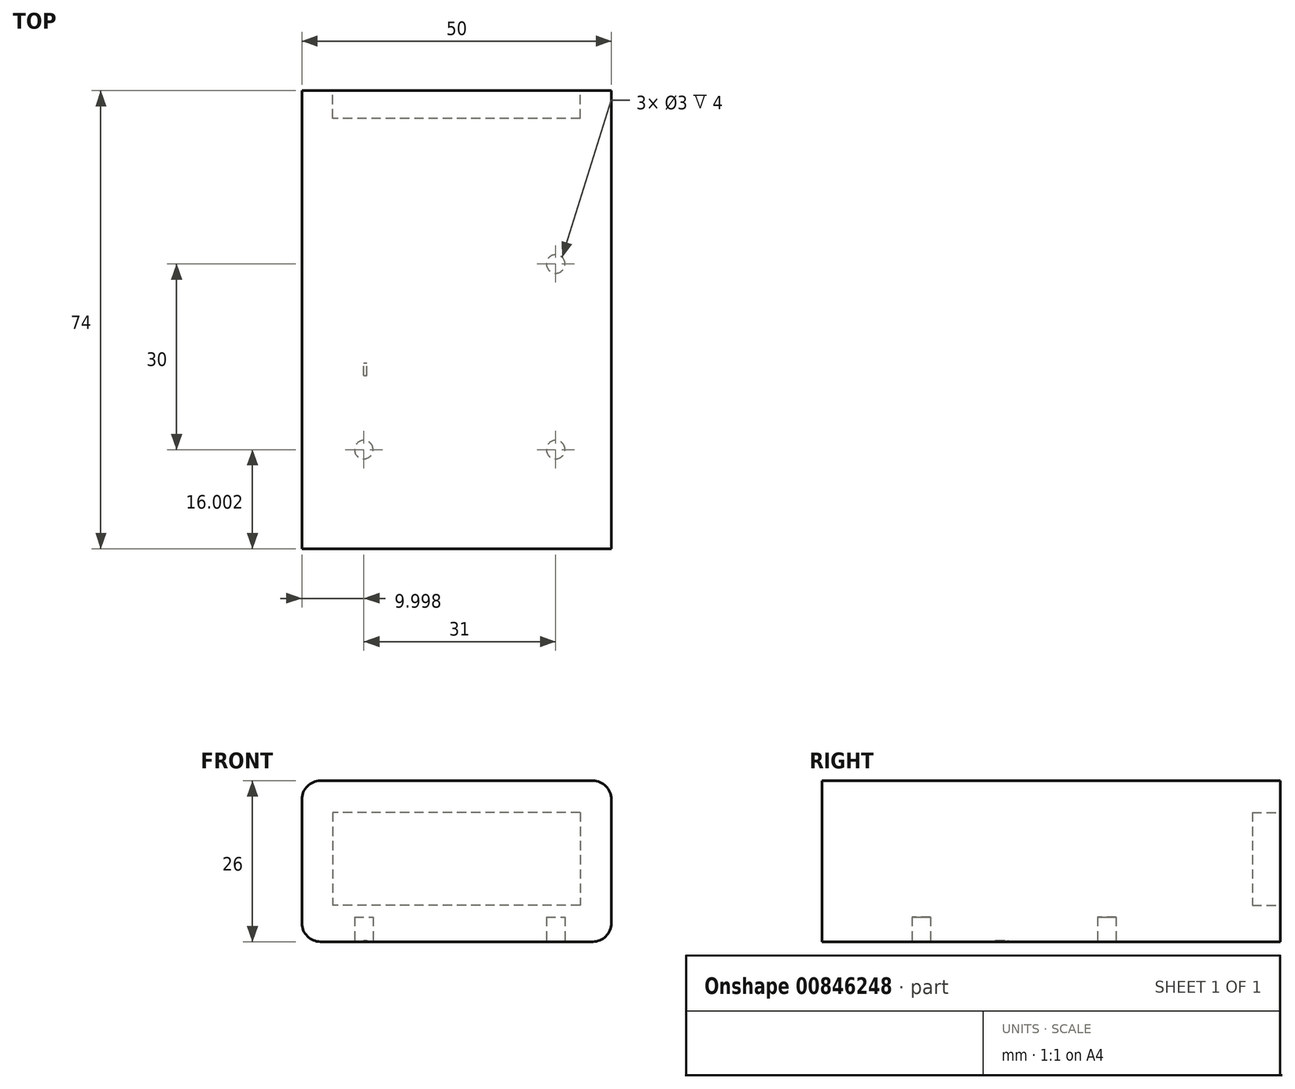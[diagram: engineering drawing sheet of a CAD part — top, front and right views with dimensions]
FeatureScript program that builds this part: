
annotation { "Feature Type Name" : "Feature", "Feature Type Description" : "" }
export const myFeature = defineFeature(function(context is Context, id is Id, definition is map)
    precondition{}
    {
        {
            var Q0;
            Q0=qCreatedBy(makeId("Top.planeOp"),FACE);
            var sketch = newSketch(context, id + "F0", { "sketchPlane" : qUnion([Q0])});
            skLineSegment(sketch, "E0.bottom", {"start": v(-22.9, 37.62) * mm, "end": v(27.1, 37.62) * mm});
            skLineSegment(sketch, "E0.top", {"start": v(-22.9, -36.38) * mm, "end": v(27.1, -36.38) * mm});
            skLineSegment(sketch, "E0.left", {"start": v(-22.9, 37.62) * mm, "end": v(-22.9, -36.38) * mm});
            skLineSegment(sketch, "E0.right", {"start": v(27.1, 37.62) * mm, "end": v(27.1, -36.38) * mm});
            skSolve(sketch);
        }
        {
            var Q0;
            Q0 = qSketchRegion(id + "F0", true);
            extrude(context, id + "F1", {"entities" : qUnion([Q0]), "depth" : 26 * mm, "offsetDistance" : 25 * mm});
        }
        {
            var Q0;
            Q0=makeQuery(id+"F1.opExtrude","SWEPT_FACE",FACE,{"disambiguationData":[OSD([sQuery(id+"F0.wireOp",EDGE,"E0.bottom")])]});
            var sketch = newSketch(context, id + "F2", { "sketchPlane" : qUnion([Q0])});
            skLineSegment(sketch, "E1.bottom", {"start": v(-22.05, 20.89) * mm, "end": v(17.95, 20.89) * mm});
            skLineSegment(sketch, "E1.top", {"start": v(-22.05, 5.89) * mm, "end": v(17.95, 5.89) * mm});
            skLineSegment(sketch, "E1.left", {"start": v(-22.05, 20.89) * mm, "end": v(-22.05, 5.89) * mm});
            skLineSegment(sketch, "E1.right", {"start": v(17.95, 20.89) * mm, "end": v(17.95, 5.89) * mm});
            skSolve(sketch);
        }
        {
            var Q0;
            Q0 = qSketchRegion(id + "F2", true);
            extrude(context, id + "F3", {"entities" : qUnion([Q0]), "operationType" : NewBodyOperationType.REMOVE, "oppositeDirection" : true, "depth" : 4.5 * mm, "offsetDistance" : 25 * mm});
        }
        {
            var Q0;
            Q0=makeQuery(id+"F1.opExtrude","CAP_FACE",FACE,{"disambiguationData":[OSD([sQuery(id+"F0.wireOp",EDGE,"E0.bottom"),sQuery(id+"F0.wireOp",EDGE,"E0.top"),sQuery(id+"F0.wireOp",EDGE,"E0.left"),sQuery(id+"F0.wireOp",EDGE,"E0.right")])],"isStart":true});
            var sketch = newSketch(context, id + "F4", { "sketchPlane" : qUnion([Q0])});
            skLineSegment(sketch, "E2", {"start": v(18.1, -37.62) * mm, "end": v(18.1, -9.62) * mm});
            skLineSegment(sketch, "E3", {"start": v(18.1, -9.62) * mm, "end": v(18.1, 20.38) * mm});
            skLineSegment(sketch, "E4", {"start": v(18.1, 20.38) * mm, "end": v(-12.9, 20.38) * mm});
            skCircle(sketch, "E5", {"center": v(18.1, 20.38) * mm, "radius": 1.5 * mm});
            skCircle(sketch, "E6", {"center": v(-12.9, 20.38) * mm, "radius": 1.5 * mm});
            skCircle(sketch, "E7", {"center": v(18.1, -9.62) * mm, "radius": 1.5 * mm});
            skCircle(sketch, "E8", {"center": v(18.1, -9.62) * mm, "radius": 2.25 * mm});
            skCircle(sketch, "E9", {"center": v(18.1, 20.38) * mm, "radius": 2.25 * mm});
            skCircle(sketch, "E10", {"center": v(-12.9, 20.38) * mm, "radius": 2.25 * mm});
            skLineSegment(sketch, "E11", {"start": v(-12.9, 20.38) * mm, "end": v(-12.9, 8.38) * mm});
            skLineSegment(sketch, "E12.bottom", {"start": v(-12.9, 8.38) * mm, "end": v(-12.4, 8.38) * mm});
            skLineSegment(sketch, "E12.top", {"start": v(-12.9, 6.38) * mm, "end": v(-12.4, 6.38) * mm});
            skLineSegment(sketch, "E12.left", {"start": v(-12.9, 8.38) * mm, "end": v(-12.9, 6.38) * mm});
            skLineSegment(sketch, "E12.right", {"start": v(-12.4, 8.38) * mm, "end": v(-12.4, 6.38) * mm});
            skSolve(sketch);
        }
        {
            var Q0;
            Q0=makeQuery(id+"F1.opExtrude","CAP_EDGE",EDGE,{"disambiguationData":[OSD([sQuery(id+"F0.wireOp",EDGE,"E0.right")])],"isStart":true});
            var Q1;
            Q1=makeQuery(id+"F1.opExtrude","CAP_EDGE",EDGE,{"disambiguationData":[OSD([sQuery(id+"F0.wireOp",EDGE,"E0.right")])],"isStart":false});
            var Q2;
            Q2=makeQuery(id+"F1.opExtrude","CAP_EDGE",EDGE,{"disambiguationData":[OSD([sQuery(id+"F0.wireOp",EDGE,"E0.left")])],"isStart":true});
            var Q3;
            Q3=makeQuery(id+"F1.opExtrude","CAP_EDGE",EDGE,{"disambiguationData":[OSD([sQuery(id+"F0.wireOp",EDGE,"E0.left")])],"isStart":false});
            fillet(context, id + "F5", {"entities" : qUnion([Q0, Q1, Q2, Q3]), "radius" : 3 * mm, "tangentPropagation" : true, "allowEdgeOverflow" : false});
        }
        {
            var Q0;
            {var subQ0=sQuery(id+"F4.wireOp",EDGE,"E4");var subQ1=sQuery(id+"F4.wireOp",EDGE,"E3");var subQ2=makeQuery(id+"F4.imprint","INTERSECT",VERTEX,{"derivedFrom":[subQ1,subQ0]});Q0=makeQuery(id+"F4.imprint","IMPRINT",FACE,{"disambiguationData":[TD([[makeQuery(id+"F4.imprint","IMPRINT",EDGE,{"disambiguationData":[TD([[subQ2,1.0]])],"derivedFrom":subQ1}),-1.0]])]});}
            var Q1;
            {var subQ0=sQuery(id+"F4.wireOp",EDGE,"E4");var subQ1=sQuery(id+"F4.wireOp",EDGE,"E3");var subQ2=makeQuery(id+"F4.imprint","INTERSECT",VERTEX,{"derivedFrom":[subQ1,subQ0]});Q1=makeQuery(id+"F4.imprint","IMPRINT",FACE,{"disambiguationData":[TD([[makeQuery(id+"F4.imprint","IMPRINT",EDGE,{"disambiguationData":[TD([[subQ2,1.0]])],"derivedFrom":subQ1}),1.0]])]});}
            var Q2;
            Q2=makeQuery(id+"F4.imprint","IMPRINT",FACE,{"disambiguationData":[TD([[makeQuery(id+"F4.imprint","IMPRINT",EDGE,{"derivedFrom":sQuery(id+"F4.wireOp",EDGE,"E6")}),1.0]])]});
            var Q3;
            {var subQ0=sQuery(id+"F4.wireOp",EDGE,"E3");var subQ1=sQuery(id+"F4.wireOp",EDGE,"E2");var subQ2=makeQuery(id+"F4.imprint","INTERSECT",VERTEX,{"derivedFrom":[subQ1,subQ0]});Q3=makeQuery(id+"F4.imprint","IMPRINT",FACE,{"disambiguationData":[TD([[makeQuery(id+"F4.imprint","IMPRINT",EDGE,{"disambiguationData":[TD([[subQ2,1.0]])],"derivedFrom":subQ1}),1.0]])]});}
            var Q4;
            {var subQ0=sQuery(id+"F4.wireOp",EDGE,"E3");var subQ1=sQuery(id+"F4.wireOp",EDGE,"E2");var subQ2=makeQuery(id+"F4.imprint","INTERSECT",VERTEX,{"derivedFrom":[subQ1,subQ0]});Q4=makeQuery(id+"F4.imprint","IMPRINT",FACE,{"disambiguationData":[TD([[makeQuery(id+"F4.imprint","IMPRINT",EDGE,{"disambiguationData":[TD([[subQ2,1.0]])],"derivedFrom":subQ1}),-1.0]])]});}
            extrude(context, id + "F6", {"entities" : qUnion([Q0, Q1, Q2, Q3, Q4]), "operationType" : NewBodyOperationType.REMOVE, "oppositeDirection" : true, "depth" : 4 * mm, "offsetDistance" : 25 * mm});
        }
        {
            var Q0;
            Q0=makeQuery(id+"F4.imprint","IMPRINT",FACE,{"disambiguationData":[TD([[makeQuery(id+"F4.imprint","IMPRINT",EDGE,{"derivedFrom":sQuery(id+"F4.wireOp",EDGE,"E12.bottom")}),-1.0]])]});
            extrude(context, id + "F7", {"entities" : qUnion([Q0]), "operationType" : NewBodyOperationType.REMOVE, "oppositeDirection" : true, "depth" : 0.2 * mm, "offsetDistance" : 25 * mm});
        }
    });
